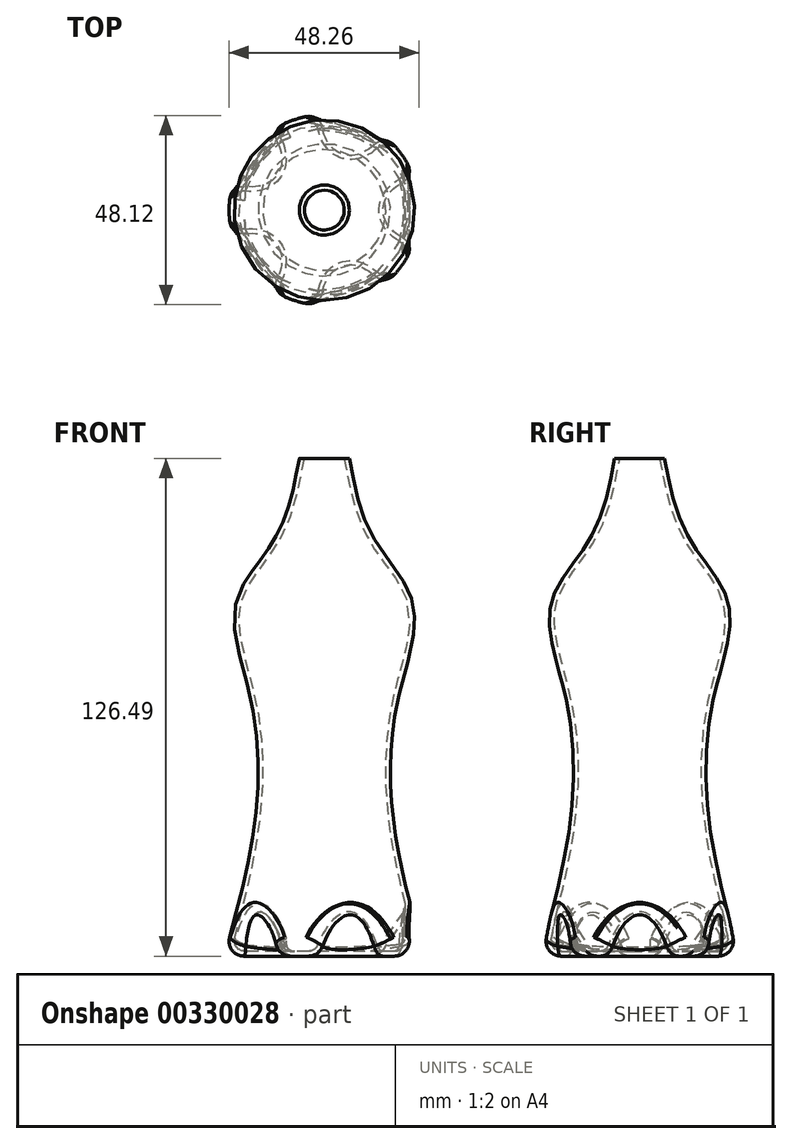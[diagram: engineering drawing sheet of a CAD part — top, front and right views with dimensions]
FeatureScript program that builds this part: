
annotation { "Feature Type Name" : "Feature", "Feature Type Description" : "" }
export const myFeature = defineFeature(function(context is Context, id is Id, definition is map)
    precondition{}
    {
        {
            var Q0;
            Q0=qCreatedBy(makeId("Top.planeOp"),FACE);
            var sketch = newSketch(context, id + "F0", { "sketchPlane" : qUnion([Q0])});
            skCircle(sketch, "E0", {"center": v(0, 0) * mm, "radius": 25.4 * mm});
            skSolve(sketch);
        }
        {
            var Q0;
            Q0=qCreatedBy(makeId("Top.planeOp"),FACE);
            cPlane(context, id + "F1", {"entities" : qUnion([Q0]), "cplaneType" : CPlaneType.OFFSET, "offset" : 25.4 * mm, "width" : 152.4 * mm, "height" : 152.4 * mm});
        }
        {
            var Q0;
            Q0=qCreatedBy(id+"F1.planeOp",FACE);
            var sketch = newSketch(context, id + "F2", { "sketchPlane" : qUnion([Q0])});
            skCircle(sketch, "E1", {"center": v(0, 0) * mm, "radius": 19.05 * mm});
            skSolve(sketch);
        }
        {
            var Q0;
            Q0=qCreatedBy(id+"F1.planeOp",FACE);
            cPlane(context, id + "F3", {"entities" : qUnion([Q0]), "cplaneType" : CPlaneType.OFFSET, "offset" : 41.4 * mm, "width" : 152.4 * mm, "height" : 152.4 * mm});
        }
        {
            var Q0;
            Q0=qCreatedBy(id+"F3.planeOp",FACE);
            var sketch = newSketch(context, id + "F4", { "sketchPlane" : qUnion([Q0])});
            skCircle(sketch, "E2", {"center": v(0, 0) * mm, "radius": 19.05 * mm});
            skSolve(sketch);
        }
        {
            var Q0;
            Q0=qCreatedBy(id+"F3.planeOp",FACE);
            cPlane(context, id + "F5", {"entities" : qUnion([Q0]), "cplaneType" : CPlaneType.OFFSET, "offset" : 23.88 * mm, "width" : 152.4 * mm, "height" : 152.4 * mm});
        }
        {
            var Q0;
            Q0=qCreatedBy(id+"F5.planeOp",FACE);
            var sketch = newSketch(context, id + "F6", { "sketchPlane" : qUnion([Q0])});
            skCircle(sketch, "E3", {"center": v(0, 0) * mm, "radius": 22.23 * mm});
            skSolve(sketch);
        }
        {
            var Q0;
            Q0=qCreatedBy(id+"F5.planeOp",FACE);
            cPlane(context, id + "F7", {"entities" : qUnion([Q0]), "cplaneType" : CPlaneType.OFFSET, "offset" : 15.24 * mm, "width" : 152.4 * mm, "height" : 152.4 * mm});
        }
        {
            var Q0;
            Q0=qCreatedBy(id+"F7.planeOp",FACE);
            var sketch = newSketch(context, id + "F8", { "sketchPlane" : qUnion([Q0])});
            skCircle(sketch, "E4", {"center": v(0, 0) * mm, "radius": 12.7 * mm});
            skSolve(sketch);
        }
        {
            var Q0;
            Q0=qCreatedBy(id+"F7.planeOp",FACE);
            cPlane(context, id + "F9", {"entities" : qUnion([Q0]), "cplaneType" : CPlaneType.OFFSET, "offset" : 20.57 * mm, "width" : 152.4 * mm, "height" : 152.4 * mm});
        }
        {
            var Q0;
            Q0=qCreatedBy(id+"F9.planeOp",FACE);
            var sketch = newSketch(context, id + "F10", { "sketchPlane" : qUnion([Q0])});
            skCircle(sketch, "E5", {"center": v(0, 0) * mm, "radius": 6.35 * mm});
            skSolve(sketch);
        }
        {
            var Q0;
            Q0=makeQuery(id+"F0.imprint","IMPRINT",FACE,{"disambiguationData":[TD([[makeQuery(id+"F0.imprint","IMPRINT",EDGE,{"derivedFrom":sQuery(id+"F0.wireOp",EDGE,"E0")}),1.0]])]});
            var Q1;
            Q1=makeQuery(id+"F2.imprint","IMPRINT",FACE,{"disambiguationData":[TD([[makeQuery(id+"F2.imprint","IMPRINT",EDGE,{"derivedFrom":sQuery(id+"F2.wireOp",EDGE,"E1")}),1.0]])]});
            var Q2;
            Q2=makeQuery(id+"F4.imprint","IMPRINT",FACE,{"disambiguationData":[TD([[makeQuery(id+"F4.imprint","IMPRINT",EDGE,{"derivedFrom":sQuery(id+"F4.wireOp",EDGE,"E2")}),1.0]])]});
            var Q3;
            Q3=makeQuery(id+"F6.imprint","IMPRINT",FACE,{"disambiguationData":[TD([[makeQuery(id+"F6.imprint","IMPRINT",EDGE,{"derivedFrom":sQuery(id+"F6.wireOp",EDGE,"E3")}),1.0]])]});
            var Q4;
            Q4=makeQuery(id+"F8.imprint","IMPRINT",FACE,{"disambiguationData":[TD([[makeQuery(id+"F8.imprint","IMPRINT",EDGE,{"derivedFrom":sQuery(id+"F8.wireOp",EDGE,"E4")}),1.0]])]});
            var Q5;
            Q5=makeQuery(id+"F10.imprint","IMPRINT",FACE,{"disambiguationData":[TD([[makeQuery(id+"F10.imprint","IMPRINT",EDGE,{"derivedFrom":sQuery(id+"F10.wireOp",EDGE,"E5")}),1.0]])]});
            loft(context, id + "F11", {"sheetProfilesArray" : [{ "sheetProfileEntities" : qUnion([Q0]) }, { "sheetProfileEntities" : qUnion([Q1]) }, { "sheetProfileEntities" : qUnion([Q2]) }, { "sheetProfileEntities" : qUnion([Q3]) }, { "sheetProfileEntities" : qUnion([Q4]) }, { "sheetProfileEntities" : qUnion([Q5]) }]});
        }
        {
            var Q0;
            Q0=qCreatedBy(makeId("Top.planeOp"),FACE);
            var sketch = newSketch(context, id + "F12", { "sketchPlane" : qUnion([Q0])});
            skLineSegment(sketch, "E6", {"start": v(24.99, -73.25) * mm, "end": v(24.99, 54.24) * mm, "construction": true});
            skSolve(sketch);
        }
        {
            var Q0;
            Q0=qCreatedBy(makeId("Top.planeOp"),FACE);
            var Q1;
            Q1=sQuery(id+"F12.wireOp",EDGE,"E6");
            cPlane(context, id + "F13", {"entities" : qUnion([Q0, Q1]), "cplaneType" : CPlaneType.LINE_ANGLE, "offset" : 25.4 * mm, "angle" : 35 * degree, "width" : 152.4 * mm, "height" : 152.4 * mm});
        }
        {
            var Q0;
            Q0=qCreatedBy(id+"F13.planeOp",FACE);
            var sketch = newSketch(context, id + "F14", { "sketchPlane" : qUnion([Q0])});
            skCircle(sketch, "E7", {"center": v(19.98, 0) * mm, "radius": 8.7 * mm});
            skSolve(sketch);
        }
        {
            var Q0;
            Q0=qCreatedBy(makeId("Front.planeOp"),FACE);
            var sketch = newSketch(context, id + "F15", { "sketchPlane" : qUnion([Q0])});
            skLineSegment(sketch, "E8", {"start": v(0, 72.32) * mm, "end": v(0, -54.4) * mm, "construction": true});
            skSolve(sketch);
        }
        {
            var Q0;
            Q0=makeQuery(id+"F14.imprint","IMPRINT",FACE,{"disambiguationData":[TD([[makeQuery(id+"F14.imprint","IMPRINT",EDGE,{"derivedFrom":sQuery(id+"F14.wireOp",EDGE,"E7")}),1.0]])]});
            extrude(context, id + "F16", {"entities" : qUnion([Q0]), "endBound" : BoundingType.SYMMETRIC, "oppositeDirection" : true, "depth" : 36.58 * mm});
        }
        {
            var Q0;
            Q0=makeQuery(id+"F16.opExtrude","SWEPT_BODY",BODY,{"disambiguationData":[OSD([sQuery(id+"F14.wireOp",EDGE,"E7")])]});
            var Q1;
            Q1=sQuery(id+"F15.wireOp",EDGE,"E8");
            circularPattern(context, id + "F17", {"operationType" : NewBodyOperationType.REMOVE, "entities" : qUnion([Q0]), "axis" : qUnion([Q1]), "angle" : 360 * degree, "instanceCount" : 5, "equalSpace" : true});
        }
        {
            var Q0;
            Q0=makeQuery(id+"F17.boolean.opBoolean","INTERSECT",EDGE,{"derivedFrom":[makeQuery(id+"F11.opLoft","SWEPT_FACE",FACE,{"disambiguationData":[OSD([sQuery(id+"F0.wireOp",EDGE,"E0"),sQuery(id+"F2.wireOp",EDGE,"E1")])]}),makeQuery(id+"F17.opPattern","COPY",FACE,{"derivedFrom":makeQuery(id+"F16.opExtrude","SWEPT_FACE",FACE,{"disambiguationData":[OSD([sQuery(id+"F14.wireOp",EDGE,"E7")])]}),"instanceName":"4"})]});
            var Q1;
            Q1=makeQuery(id+"F17.boolean.opBoolean","INTERSECT",EDGE,{"derivedFrom":[makeQuery(id+"F11.opLoft","CAP_FACE",FACE,{"disambiguationData":[OSD([makeQuery(id+"F0.imprint","IMPRINT",FACE,{"disambiguationData":[TD([[makeQuery(id+"F0.imprint","IMPRINT",EDGE,{"derivedFrom":sQuery(id+"F0.wireOp",EDGE,"E0")}),1.0]])]})])],"isStart":true}),makeQuery(id+"F17.opPattern","COPY",FACE,{"derivedFrom":makeQuery(id+"F16.opExtrude","SWEPT_FACE",FACE,{"disambiguationData":[OSD([sQuery(id+"F14.wireOp",EDGE,"E7")])]}),"instanceName":"4"})]});
            var Q2;
            {var subQ0=sQuery(id+"F0.wireOp",EDGE,"E0");var subQ1=makeQuery(id+"F16.opExtrude","SWEPT_FACE",FACE,{"disambiguationData":[OSD([sQuery(id+"F14.wireOp",EDGE,"E7")])]});Q2=makeQuery(id+"F17.boolean.opBoolean","SPLIT",EDGE,{"disambiguationData":[TD([makeQuery(id+"F11.opLoft","SWEPT_FACE",FACE,{"disambiguationData":[OSD([subQ0,sQuery(id+"F2.wireOp",EDGE,"E1")])]}),makeQuery(id+"F11.opLoft","CAP_FACE",FACE,{"disambiguationData":[OSD([makeQuery(id+"F0.imprint","IMPRINT",FACE,{"disambiguationData":[TD([[makeQuery(id+"F0.imprint","IMPRINT",EDGE,{"derivedFrom":subQ0}),1.0]])]})])],"isStart":true}),subQ1,makeQuery(id+"F17.opPattern","COPY",FACE,{"derivedFrom":subQ1,"instanceName":"4"})])],"derivedFrom":makeQuery(id+"F11.opLoft","MID_CAP_EDGE",EDGE,{"disambiguationData":[OSD([subQ0])],"capPos":0.0})});}
            var Q3;
            Q3=makeQuery(id+"F17.boolean.opBoolean","INTERSECT",EDGE,{"derivedFrom":[makeQuery(id+"F11.opLoft","SWEPT_FACE",FACE,{"disambiguationData":[OSD([sQuery(id+"F0.wireOp",EDGE,"E0"),sQuery(id+"F2.wireOp",EDGE,"E1")])]}),makeQuery(id+"F16.opExtrude","SWEPT_FACE",FACE,{"disambiguationData":[OSD([sQuery(id+"F14.wireOp",EDGE,"E7")])]})]});
            var Q4;
            Q4=makeQuery(id+"F17.boolean.opBoolean","INTERSECT",EDGE,{"derivedFrom":[makeQuery(id+"F11.opLoft","CAP_FACE",FACE,{"disambiguationData":[OSD([makeQuery(id+"F0.imprint","IMPRINT",FACE,{"disambiguationData":[TD([[makeQuery(id+"F0.imprint","IMPRINT",EDGE,{"derivedFrom":sQuery(id+"F0.wireOp",EDGE,"E0")}),1.0]])]})])],"isStart":true}),makeQuery(id+"F16.opExtrude","SWEPT_FACE",FACE,{"disambiguationData":[OSD([sQuery(id+"F14.wireOp",EDGE,"E7")])]})]});
            var Q5;
            Q5=makeQuery(id+"F17.boolean.opBoolean","INTERSECT",EDGE,{"derivedFrom":[makeQuery(id+"F11.opLoft","CAP_FACE",FACE,{"disambiguationData":[OSD([makeQuery(id+"F0.imprint","IMPRINT",FACE,{"disambiguationData":[TD([[makeQuery(id+"F0.imprint","IMPRINT",EDGE,{"derivedFrom":sQuery(id+"F0.wireOp",EDGE,"E0")}),1.0]])]})])],"isStart":true}),makeQuery(id+"F17.opPattern","COPY",FACE,{"derivedFrom":makeQuery(id+"F16.opExtrude","SWEPT_FACE",FACE,{"disambiguationData":[OSD([sQuery(id+"F14.wireOp",EDGE,"E7")])]}),"instanceName":"1"})]});
            var Q6;
            {var subQ0=sQuery(id+"F0.wireOp",EDGE,"E0");var subQ1=makeQuery(id+"F16.opExtrude","SWEPT_FACE",FACE,{"disambiguationData":[OSD([sQuery(id+"F14.wireOp",EDGE,"E7")])]});Q6=makeQuery(id+"F17.boolean.opBoolean","SPLIT",EDGE,{"disambiguationData":[TD([makeQuery(id+"F11.opLoft","SWEPT_FACE",FACE,{"disambiguationData":[OSD([subQ0,sQuery(id+"F2.wireOp",EDGE,"E1")])]}),makeQuery(id+"F11.opLoft","CAP_FACE",FACE,{"disambiguationData":[OSD([makeQuery(id+"F0.imprint","IMPRINT",FACE,{"disambiguationData":[TD([[makeQuery(id+"F0.imprint","IMPRINT",EDGE,{"derivedFrom":subQ0}),1.0]])]})])],"isStart":true}),subQ1,makeQuery(id+"F17.opPattern","COPY",FACE,{"derivedFrom":subQ1,"instanceName":"1"})])],"derivedFrom":makeQuery(id+"F11.opLoft","MID_CAP_EDGE",EDGE,{"disambiguationData":[OSD([subQ0])],"capPos":0.0})});}
            var Q7;
            Q7=makeQuery(id+"F17.boolean.opBoolean","INTERSECT",EDGE,{"derivedFrom":[makeQuery(id+"F11.opLoft","SWEPT_FACE",FACE,{"disambiguationData":[OSD([sQuery(id+"F0.wireOp",EDGE,"E0"),sQuery(id+"F2.wireOp",EDGE,"E1")])]}),makeQuery(id+"F17.opPattern","COPY",FACE,{"derivedFrom":makeQuery(id+"F16.opExtrude","SWEPT_FACE",FACE,{"disambiguationData":[OSD([sQuery(id+"F14.wireOp",EDGE,"E7")])]}),"instanceName":"1"})]});
            var Q8;
            {var subQ0=sQuery(id+"F0.wireOp",EDGE,"E0");var subQ1=makeQuery(id+"F16.opExtrude","SWEPT_FACE",FACE,{"disambiguationData":[OSD([sQuery(id+"F14.wireOp",EDGE,"E7")])]});Q8=makeQuery(id+"F17.boolean.opBoolean","SPLIT",EDGE,{"disambiguationData":[TD([makeQuery(id+"F11.opLoft","SWEPT_FACE",FACE,{"disambiguationData":[OSD([subQ0,sQuery(id+"F2.wireOp",EDGE,"E1")])]}),makeQuery(id+"F11.opLoft","CAP_FACE",FACE,{"disambiguationData":[OSD([makeQuery(id+"F0.imprint","IMPRINT",FACE,{"disambiguationData":[TD([[makeQuery(id+"F0.imprint","IMPRINT",EDGE,{"derivedFrom":subQ0}),1.0]])]})])],"isStart":true}),makeQuery(id+"F17.opPattern","COPY",FACE,{"derivedFrom":subQ1,"instanceName":"1"}),makeQuery(id+"F17.opPattern","COPY",FACE,{"derivedFrom":subQ1,"instanceName":"2"})])],"derivedFrom":makeQuery(id+"F11.opLoft","MID_CAP_EDGE",EDGE,{"disambiguationData":[OSD([subQ0])],"capPos":0.0})});}
            var Q9;
            Q9=makeQuery(id+"F17.boolean.opBoolean","INTERSECT",EDGE,{"derivedFrom":[makeQuery(id+"F11.opLoft","SWEPT_FACE",FACE,{"disambiguationData":[OSD([sQuery(id+"F0.wireOp",EDGE,"E0"),sQuery(id+"F2.wireOp",EDGE,"E1")])]}),makeQuery(id+"F17.opPattern","COPY",FACE,{"derivedFrom":makeQuery(id+"F16.opExtrude","SWEPT_FACE",FACE,{"disambiguationData":[OSD([sQuery(id+"F14.wireOp",EDGE,"E7")])]}),"instanceName":"2"})]});
            var Q10;
            Q10=makeQuery(id+"F17.boolean.opBoolean","INTERSECT",EDGE,{"derivedFrom":[makeQuery(id+"F11.opLoft","CAP_FACE",FACE,{"disambiguationData":[OSD([makeQuery(id+"F0.imprint","IMPRINT",FACE,{"disambiguationData":[TD([[makeQuery(id+"F0.imprint","IMPRINT",EDGE,{"derivedFrom":sQuery(id+"F0.wireOp",EDGE,"E0")}),1.0]])]})])],"isStart":true}),makeQuery(id+"F17.opPattern","COPY",FACE,{"derivedFrom":makeQuery(id+"F16.opExtrude","SWEPT_FACE",FACE,{"disambiguationData":[OSD([sQuery(id+"F14.wireOp",EDGE,"E7")])]}),"instanceName":"2"})]});
            var Q11;
            {var subQ0=sQuery(id+"F0.wireOp",EDGE,"E0");var subQ1=makeQuery(id+"F16.opExtrude","SWEPT_FACE",FACE,{"disambiguationData":[OSD([sQuery(id+"F14.wireOp",EDGE,"E7")])]});Q11=makeQuery(id+"F17.boolean.opBoolean","SPLIT",EDGE,{"disambiguationData":[TD([makeQuery(id+"F11.opLoft","SWEPT_FACE",FACE,{"disambiguationData":[OSD([subQ0,sQuery(id+"F2.wireOp",EDGE,"E1")])]}),makeQuery(id+"F11.opLoft","CAP_FACE",FACE,{"disambiguationData":[OSD([makeQuery(id+"F0.imprint","IMPRINT",FACE,{"disambiguationData":[TD([[makeQuery(id+"F0.imprint","IMPRINT",EDGE,{"derivedFrom":subQ0}),1.0]])]})])],"isStart":true}),makeQuery(id+"F17.opPattern","COPY",FACE,{"derivedFrom":subQ1,"instanceName":"2"}),makeQuery(id+"F17.opPattern","COPY",FACE,{"derivedFrom":subQ1,"instanceName":"3"})])],"derivedFrom":makeQuery(id+"F11.opLoft","MID_CAP_EDGE",EDGE,{"disambiguationData":[OSD([subQ0])],"capPos":0.0})});}
            var Q12;
            Q12=makeQuery(id+"F17.boolean.opBoolean","INTERSECT",EDGE,{"derivedFrom":[makeQuery(id+"F11.opLoft","CAP_FACE",FACE,{"disambiguationData":[OSD([makeQuery(id+"F0.imprint","IMPRINT",FACE,{"disambiguationData":[TD([[makeQuery(id+"F0.imprint","IMPRINT",EDGE,{"derivedFrom":sQuery(id+"F0.wireOp",EDGE,"E0")}),1.0]])]})])],"isStart":true}),makeQuery(id+"F17.opPattern","COPY",FACE,{"derivedFrom":makeQuery(id+"F16.opExtrude","SWEPT_FACE",FACE,{"disambiguationData":[OSD([sQuery(id+"F14.wireOp",EDGE,"E7")])]}),"instanceName":"3"})]});
            var Q13;
            {var subQ0=sQuery(id+"F0.wireOp",EDGE,"E0");var subQ1=makeQuery(id+"F16.opExtrude","SWEPT_FACE",FACE,{"disambiguationData":[OSD([sQuery(id+"F14.wireOp",EDGE,"E7")])]});Q13=makeQuery(id+"F17.boolean.opBoolean","SPLIT",EDGE,{"disambiguationData":[TD([makeQuery(id+"F11.opLoft","SWEPT_FACE",FACE,{"disambiguationData":[OSD([subQ0,sQuery(id+"F2.wireOp",EDGE,"E1")])]}),makeQuery(id+"F11.opLoft","CAP_FACE",FACE,{"disambiguationData":[OSD([makeQuery(id+"F0.imprint","IMPRINT",FACE,{"disambiguationData":[TD([[makeQuery(id+"F0.imprint","IMPRINT",EDGE,{"derivedFrom":subQ0}),1.0]])]})])],"isStart":true}),makeQuery(id+"F17.opPattern","COPY",FACE,{"derivedFrom":subQ1,"instanceName":"3"}),makeQuery(id+"F17.opPattern","COPY",FACE,{"derivedFrom":subQ1,"instanceName":"4"})])],"derivedFrom":makeQuery(id+"F11.opLoft","MID_CAP_EDGE",EDGE,{"disambiguationData":[OSD([subQ0])],"capPos":0.0})});}
            var Q14;
            Q14=makeQuery(id+"F17.boolean.opBoolean","COPY",FACE,{"derivedFrom":makeQuery(id+"F17.opPattern","COPY",FACE,{"derivedFrom":makeQuery(id+"F16.opExtrude","SWEPT_FACE",FACE,{"disambiguationData":[OSD([sQuery(id+"F14.wireOp",EDGE,"E7")])]}),"instanceName":"3"})});
            fillet(context, id + "F18", {"entities" : qUnion([Q0, Q1, Q2, Q3, Q4, Q5, Q6, Q7, Q8, Q9, Q10, Q11, Q12, Q13, Q14]), "radius" : 3.8 * mm, "tangentPropagation" : true, "allowEdgeOverflow" : false});
        }
        {
            var Q0;
            Q0=makeQuery(id+"F11.opLoft","CAP_FACE",FACE,{"disambiguationData":[OSD([makeQuery(id+"F10.imprint","IMPRINT",FACE,{"disambiguationData":[TD([[makeQuery(id+"F10.imprint","IMPRINT",EDGE,{"derivedFrom":sQuery(id+"F10.wireOp",EDGE,"E5")}),1.0]])]})])],"isStart":true});
            shell(context, id + "F19", {"entities" : qUnion([Q0]), "thickness" : 1.27 * mm});
        }
    });
